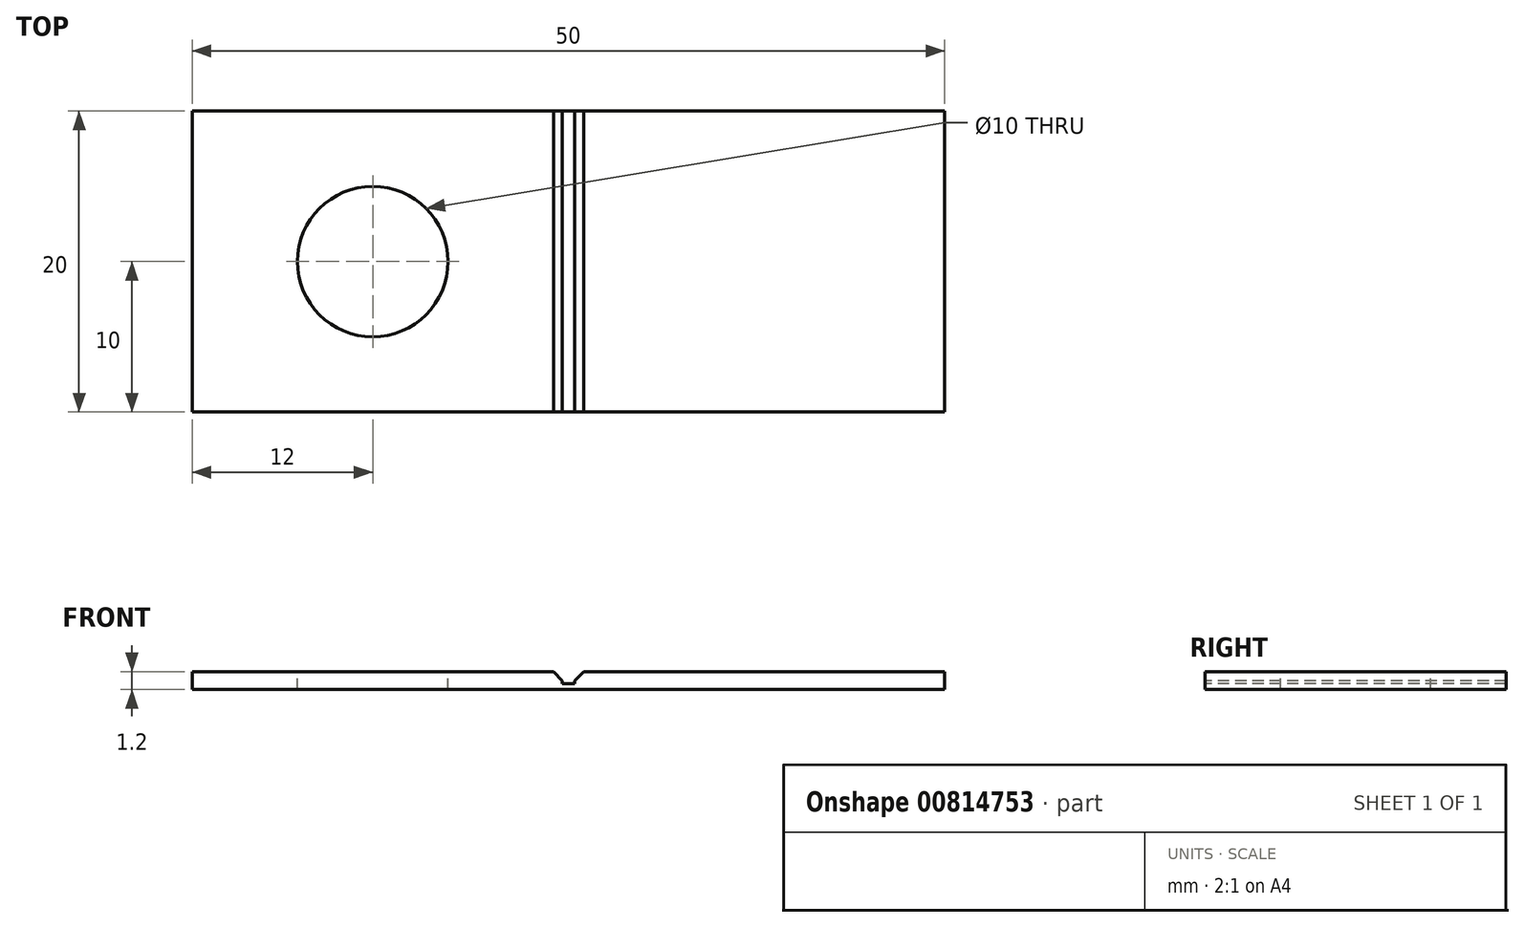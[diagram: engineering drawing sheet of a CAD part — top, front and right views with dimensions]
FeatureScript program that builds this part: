
annotation { "Feature Type Name" : "Feature", "Feature Type Description" : "" }
export const myFeature = defineFeature(function(context is Context, id is Id, definition is map)
    precondition{}
    {
        {
            var Q0;
            Q0=qCreatedBy(makeId("Top.planeOp"),FACE);
            var sketch = newSketch(context, id + "F0", { "sketchPlane" : qUnion([Q0])});
            skLineSegment(sketch, "E0.bottom", {"start": v(-25, 10) * mm, "end": v(25, 10) * mm});
            skLineSegment(sketch, "E0.top", {"start": v(-25, -10) * mm, "end": v(25, -10) * mm});
            skLineSegment(sketch, "E0.left", {"start": v(-25, 10) * mm, "end": v(-25, -10) * mm});
            skLineSegment(sketch, "E0.right", {"start": v(25, 10) * mm, "end": v(25, -10) * mm});
            skPoint(sketch, "E0.middle", {"position": v(0, 0) * mm});
            skSolve(sketch);
        }
        {
            var Q0;
            Q0=makeQuery(id+"F0.imprint","IMPRINT",FACE,{"disambiguationData":[TD([[makeQuery(id+"F0.imprint","IMPRINT",EDGE,{"derivedFrom":sQuery(id+"F0.wireOp",EDGE,"E0.bottom")}),-1.0]])]});
            extrude(context, id + "F1", {"entities" : qUnion([Q0]), "depth" : 0.4 * mm, "offsetDistance" : 25 * mm});
        }
        {
            var Q0;
            Q0=makeQuery(id+"F1.opExtrude","CAP_FACE",FACE,{"disambiguationData":[OSD([sQuery(id+"F0.wireOp",EDGE,"E0.bottom"),sQuery(id+"F0.wireOp",EDGE,"E0.top"),sQuery(id+"F0.wireOp",EDGE,"E0.left"),sQuery(id+"F0.wireOp",EDGE,"E0.right")])],"isStart":false});
            var sketch = newSketch(context, id + "F2", { "sketchPlane" : qUnion([Q0])});
            skLineSegment(sketch, "E1.bottom", {"start": v(-25, 10) * mm, "end": v(25, 10) * mm});
            skLineSegment(sketch, "E1.top", {"start": v(-25, -10) * mm, "end": v(25, -10) * mm});
            skLineSegment(sketch, "E1.left", {"start": v(-25, 10) * mm, "end": v(-25, -10) * mm});
            skLineSegment(sketch, "E1.right", {"start": v(25, 10) * mm, "end": v(25, -10) * mm});
            skLineSegment(sketch, "E2.left", {"start": v(-0.4, 10) * mm, "end": v(-0.4, -10) * mm});
            skLineSegment(sketch, "E2.right", {"start": v(0.4, 10) * mm, "end": v(0.4, -10) * mm});
            skSolve(sketch);
        }
        {
            var Q0;
            {var subQ0=sQuery(id+"F2.wireOp",EDGE,"E1.left");Q0=makeQuery(id+"F2.imprint","IMPRINT",FACE,{"disambiguationData":[TD([[makeQuery(id+"F2.imprint","IMPRINT",EDGE,{"derivedFrom":subQ0}),1.0]])]});}
            var Q1;
            {var subQ0=sQuery(id+"F2.wireOp",EDGE,"E1.right");Q1=makeQuery(id+"F2.imprint","IMPRINT",FACE,{"disambiguationData":[TD([[makeQuery(id+"F2.imprint","IMPRINT",EDGE,{"derivedFrom":subQ0}),-1.0]])]});}
            extrude(context, id + "F3", {"entities" : qUnion([Q0, Q1]), "operationType" : NewBodyOperationType.ADD, "depth" : 0.8 * mm, "offsetDistance" : 25 * mm});
        }
        {
            var Q0;
            Q0=makeQuery(id+"F3.opExtrude","CAP_FACE",FACE,{"disambiguationData":[OSD([sQuery(id+"F2.wireOp",EDGE,"E1.bottom"),sQuery(id+"F2.wireOp",EDGE,"E1.top"),sQuery(id+"F2.wireOp",EDGE,"E1.left"),sQuery(id+"F2.wireOp",EDGE,"E2.left")])],"isStart":false});
            var sketch = newSketch(context, id + "F4", { "sketchPlane" : qUnion([Q0])});
            skCircle(sketch, "E3", {"center": v(-13, 0) * mm, "radius": 5 * mm});
            skSolve(sketch);
        }
        {
            var Q0;
            Q0=makeQuery(id+"F4.imprint","IMPRINT",FACE,{"disambiguationData":[TD([[makeQuery(id+"F4.imprint","IMPRINT",EDGE,{"derivedFrom":sQuery(id+"F4.wireOp",EDGE,"E3")}),1.0]])]});
            extrude(context, id + "F5", {"entities" : qUnion([Q0]), "operationType" : NewBodyOperationType.REMOVE, "oppositeDirection" : true, "depth" : 25 * mm, "offsetDistance" : 25 * mm});
        }
        {
            var Q0;
            Q0=makeQuery(id+"F3.opExtrude","CAP_EDGE",EDGE,{"disambiguationData":[OSD([sQuery(id+"F2.wireOp",EDGE,"E2.left")])],"isStart":false});
            var Q1;
            Q1=makeQuery(id+"F3.opExtrude","CAP_EDGE",EDGE,{"disambiguationData":[OSD([sQuery(id+"F2.wireOp",EDGE,"E2.right")])],"isStart":false});
            chamfer(context, id + "F6", {"entities" : qUnion([Q0, Q1]), "width" : 0.6 * mm, "tangentPropagation" : true});
        }
    });
